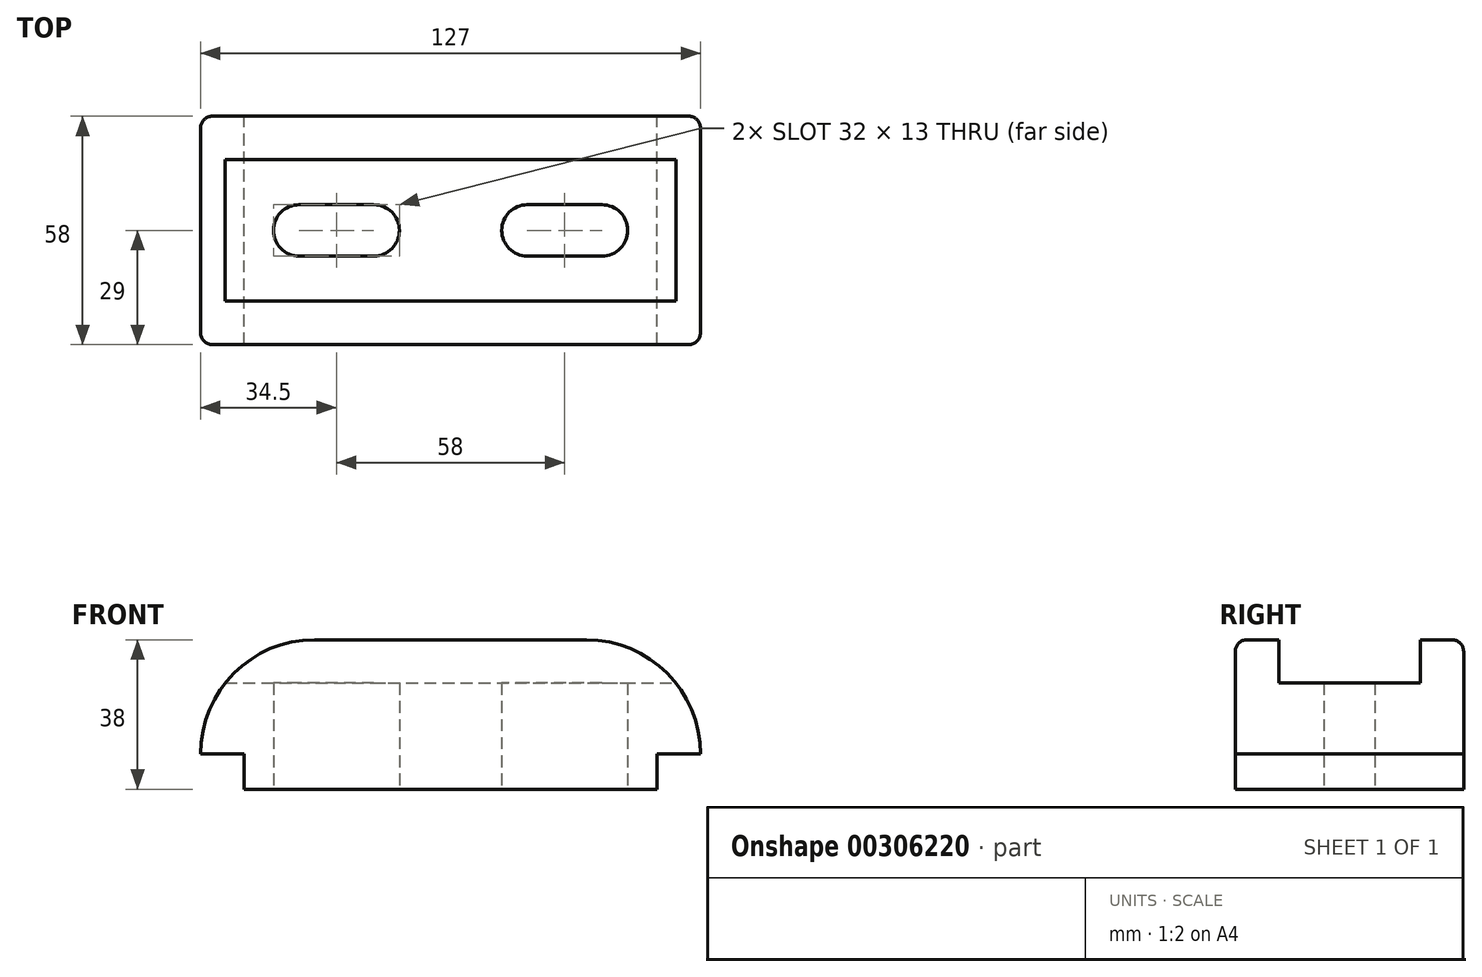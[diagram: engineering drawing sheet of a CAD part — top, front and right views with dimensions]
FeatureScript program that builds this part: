
annotation { "Feature Type Name" : "Feature", "Feature Type Description" : "" }
export const myFeature = defineFeature(function(context is Context, id is Id, definition is map)
    precondition{}
    {
        {
            var Q0;
            Q0=qCreatedBy(makeId("Front.planeOp"),FACE);
            var sketch = newSketch(context, id + "F0", { "sketchPlane" : qUnion([Q0])});
            skLineSegment(sketch, "E0", {"start": v(-52.5, 0) * mm, "end": v(52.5, 0) * mm});
            skLineSegment(sketch, "E1", {"start": v(52.5, 0) * mm, "end": v(52.5, 9) * mm});
            skLineSegment(sketch, "E2", {"start": v(52.5, 9) * mm, "end": v(63.5, 9) * mm});
            skLineSegment(sketch, "E3", {"start": v(-52.5, 0) * mm, "end": v(-52.5, 9) * mm});
            skLineSegment(sketch, "E4", {"start": v(-52.5, 9) * mm, "end": v(-63.5, 9) * mm});
            skArc(sketch, "E5", {"start": v(-63.5, 9) * mm, "mid": v(-55, 29.5) * mm, "end": v(-34.5, 38) * mm});
            skArc(sketch, "E6", {"start": v(63.5, 9) * mm, "mid": v(55, 29.5) * mm, "end": v(34.5, 38) * mm});
            skLineSegment(sketch, "E7", {"start": v(-34.5, 38) * mm, "end": v(34.5, 38) * mm});
            skLineSegment(sketch, "E8", {"start": v(-57.24, 27) * mm, "end": v(57.24, 27) * mm});
            skSolve(sketch);
        }
        {
            var Q0;
            Q0=makeQuery(id+"F0.imprint","IMPRINT",FACE,{"disambiguationData":[TD([[makeQuery(id+"F0.imprint","IMPRINT",EDGE,{"derivedFrom":sQuery(id+"F0.wireOp",EDGE,"E0")}),1.0]])]});
            var Q1;
            {var subQ0=sQuery(id+"F0.wireOp",EDGE,"E7");Q1=makeQuery(id+"F0.imprint","IMPRINT",FACE,{"disambiguationData":[TD([[makeQuery(id+"F0.imprint","IMPRINT",EDGE,{"derivedFrom":subQ0}),-1.0]])]});}
            extrude(context, id + "F1", {"entities" : qUnion([Q0, Q1]), "endBound" : BoundingType.SYMMETRIC, "depth" : 58 * mm});
        }
        {
            var Q0;
            {var subQ0=sQuery(id+"F0.wireOp",EDGE,"E7");Q0=makeQuery(id+"F0.imprint","IMPRINT",FACE,{"disambiguationData":[TD([[makeQuery(id+"F0.imprint","IMPRINT",EDGE,{"derivedFrom":subQ0}),-1.0]])]});}
            extrude(context, id + "F2", {"entities" : qUnion([Q0]), "operationType" : NewBodyOperationType.REMOVE, "endBound" : BoundingType.SYMMETRIC, "depth" : 36 * mm});
        }
        {
            var Q0;
            Q0=makeQuery(id+"F1.opExtrude","SWEPT_FACE",FACE,{"disambiguationData":[OSD([sQuery(id+"F0.wireOp",EDGE,"E0")])]});
            var sketch = newSketch(context, id + "F3", { "sketchPlane" : qUnion([Q0])});
            skLineSegment(sketch, "E9", {"start": v(-38.5, 6.5) * mm, "end": v(-19.5, 6.5) * mm});
            skLineSegment(sketch, "E10", {"start": v(-38.5, -6.5) * mm, "end": v(-19.5, -6.5) * mm});
            skLineSegment(sketch, "E11", {"start": v(19.5, 6.5) * mm, "end": v(38.5, 6.5) * mm});
            skLineSegment(sketch, "E12", {"start": v(19.5, -6.5) * mm, "end": v(38.5, -6.5) * mm});
            skArc(sketch, "E13", {"start": v(-38.5, 6.5) * mm, "mid": v(-45, 0) * mm, "end": v(-38.5, -6.5) * mm});
            skArc(sketch, "E14", {"start": v(-19.5, -6.5) * mm, "mid": v(-13, 0) * mm, "end": v(-19.5, 6.5) * mm});
            skArc(sketch, "E15", {"start": v(19.5, 6.5) * mm, "mid": v(13, 0) * mm, "end": v(19.5, -6.5) * mm});
            skArc(sketch, "E16", {"start": v(38.5, -6.5) * mm, "mid": v(45, 0) * mm, "end": v(38.5, 6.5) * mm});
            skSolve(sketch);
        }
        {
            var Q0;
            Q0=makeQuery(id+"F3.imprint","IMPRINT",FACE,{"disambiguationData":[TD([[makeQuery(id+"F3.imprint","IMPRINT",EDGE,{"derivedFrom":sQuery(id+"F3.wireOp",EDGE,"E9")}),-1.0]])]});
            var Q1;
            Q1=makeQuery(id+"F3.imprint","IMPRINT",FACE,{"disambiguationData":[TD([[makeQuery(id+"F3.imprint","IMPRINT",EDGE,{"derivedFrom":sQuery(id+"F3.wireOp",EDGE,"E11")}),-1.0]])]});
            extrude(context, id + "F4", {"entities" : qUnion([Q0, Q1]), "operationType" : NewBodyOperationType.REMOVE, "endBound" : BoundingType.THROUGH_ALL, "oppositeDirection" : true, "depth" : 25 * mm});
        }
        {
            var Q0;
            Q0=makeQuery(id+"F1.opExtrude","CAP_EDGE",EDGE,{"disambiguationData":[OSD([sQuery(id+"F0.wireOp",EDGE,"E7")])],"isStart":false});
            var Q1;
            Q1=makeQuery(id+"F1.opExtrude","CAP_EDGE",EDGE,{"disambiguationData":[OSD([sQuery(id+"F0.wireOp",EDGE,"E5")])],"isStart":false});
            var Q2;
            Q2=makeQuery(id+"F1.opExtrude","CAP_EDGE",EDGE,{"disambiguationData":[OSD([sQuery(id+"F0.wireOp",EDGE,"E6")])],"isStart":true});
            var Q3;
            Q3=makeQuery(id+"F1.opExtrude","CAP_EDGE",EDGE,{"disambiguationData":[OSD([sQuery(id+"F0.wireOp",EDGE,"E5")])],"isStart":true});
            fillet(context, id + "F5", {"entities" : qUnion([Q0, Q1, Q2, Q3]), "radius" : 3 * mm, "tangentPropagation" : true, "allowEdgeOverflow" : false});
        }
    });
